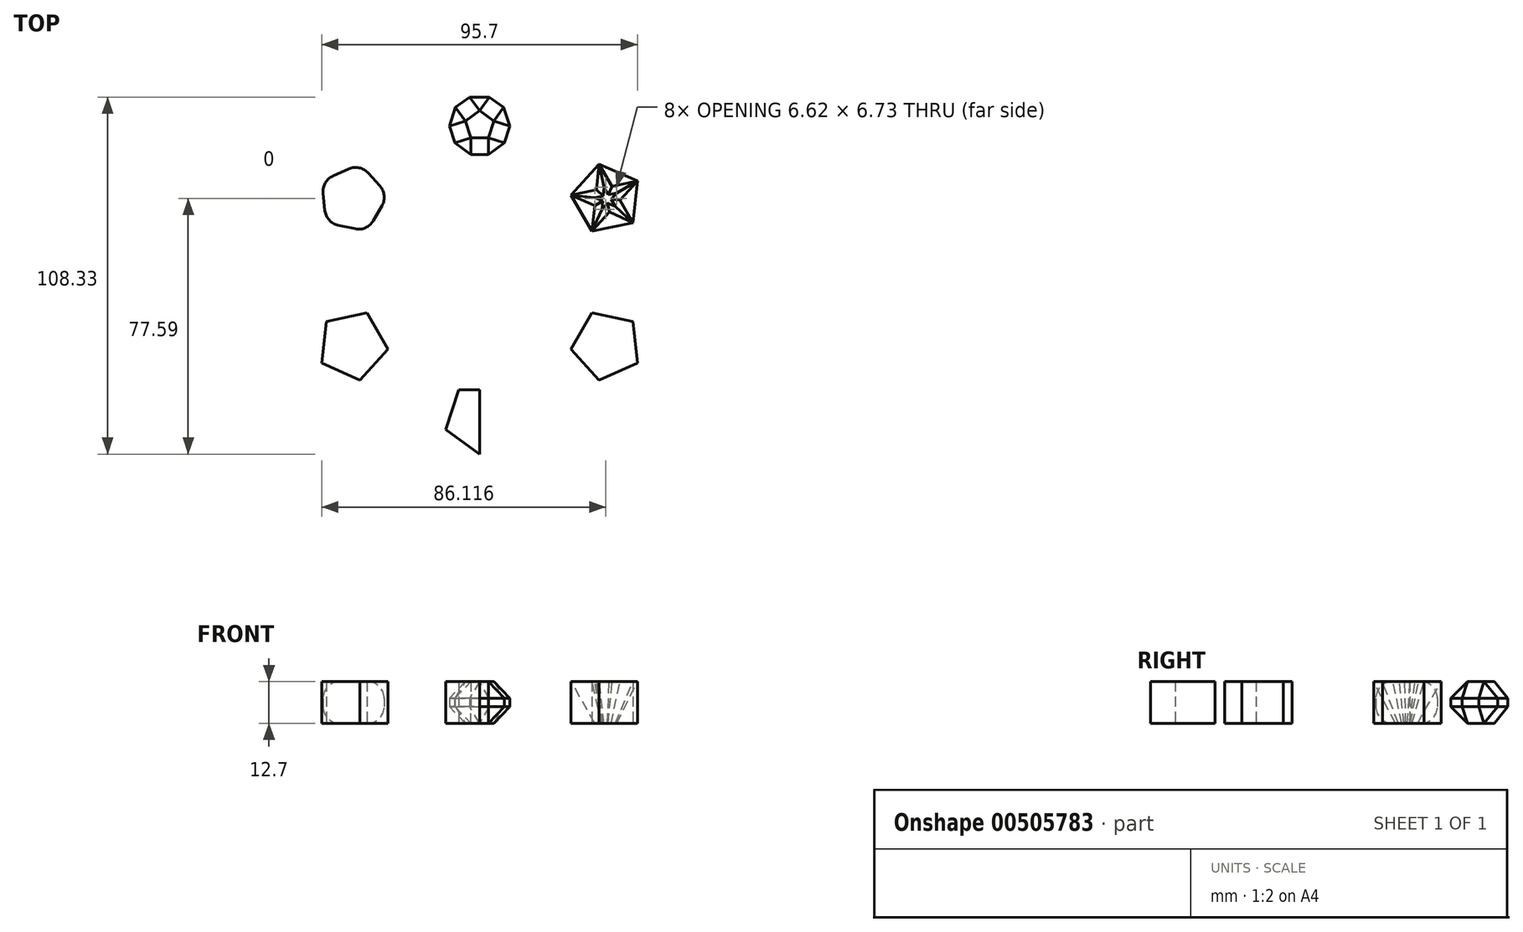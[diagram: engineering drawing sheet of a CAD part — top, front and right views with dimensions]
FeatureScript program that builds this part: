
annotation { "Feature Type Name" : "Feature", "Feature Type Description" : "" }
export const myFeature = defineFeature(function(context is Context, id is Id, definition is map)
    precondition{}
    {
        {
            var Q0;
            Q0=qCreatedBy(makeId("Top.planeOp"),FACE);
            var sketch = newSketch(context, id + "F0", { "sketchPlane" : qUnion([Q0])});
            skCircle(sketch, "E0", {"center": v(0, 0) * mm, "radius": 44.45 * mm, "construction": true});
            skCircle(sketch, "E1.cCircle", {"center": v(0, 44.45) * mm, "radius": 10.8 * mm, "construction": true});
            skLineSegment(sketch, "E1.0", {"start": v(0, 55.25) * mm, "end": v(10.27, 47.79) * mm});
            skLineSegment(sketch, "E1.1", {"start": v(10.27, 47.79) * mm, "end": v(6.35, 35.7) * mm});
            skLineSegment(sketch, "E1.2", {"start": v(6.35, 35.7) * mm, "end": v(-6.35, 35.7) * mm});
            skLineSegment(sketch, "E1.3", {"start": v(-6.35, 35.7) * mm, "end": v(-10.27, 47.79) * mm});
            skLineSegment(sketch, "E1.4", {"start": v(-10.27, 47.79) * mm, "end": v(0, 55.25) * mm});
            skLineSegment(sketch, "E2.1.0", {"start": v(-47.85, 27.63) * mm, "end": v(-36.25, 32.8) * mm});
            skLineSegment(sketch, "E2.1.1", {"start": v(-46.52, 15) * mm, "end": v(-47.85, 27.63) * mm});
            skLineSegment(sketch, "E2.1.2", {"start": v(-34.1, 12.36) * mm, "end": v(-46.52, 15) * mm});
            skLineSegment(sketch, "E2.1.3", {"start": v(-27.75, 23.35) * mm, "end": v(-34.1, 12.36) * mm});
            skLineSegment(sketch, "E2.1.4", {"start": v(-36.25, 32.8) * mm, "end": v(-27.75, 23.35) * mm});
            skLineSegment(sketch, "E2.2.0", {"start": v(-47.85, -27.63) * mm, "end": v(-46.52, -15) * mm});
            skLineSegment(sketch, "E2.2.1", {"start": v(-36.25, -32.8) * mm, "end": v(-47.85, -27.63) * mm});
            skLineSegment(sketch, "E2.2.2", {"start": v(-27.75, -23.35) * mm, "end": v(-36.25, -32.8) * mm});
            skLineSegment(sketch, "E2.2.3", {"start": v(-34.1, -12.36) * mm, "end": v(-27.75, -23.35) * mm});
            skLineSegment(sketch, "E2.2.4", {"start": v(-46.52, -15) * mm, "end": v(-34.1, -12.36) * mm});
            skLineSegment(sketch, "E2.3.0", {"start": v(0, -55.25) * mm, "end": v(-10.27, -47.79) * mm});
            skLineSegment(sketch, "E2.3.4", {"start": v(-10.27, -47.79) * mm, "end": v(-6.35, -35.7) * mm});
            skLineSegment(sketch, "E2.4.0", {"start": v(47.85, -27.63) * mm, "end": v(36.25, -32.8) * mm});
            skLineSegment(sketch, "E2.4.1", {"start": v(46.52, -15) * mm, "end": v(47.85, -27.63) * mm});
            skLineSegment(sketch, "E2.4.2", {"start": v(34.1, -12.36) * mm, "end": v(46.52, -15) * mm});
            skLineSegment(sketch, "E2.4.3", {"start": v(27.75, -23.35) * mm, "end": v(34.1, -12.36) * mm});
            skLineSegment(sketch, "E2.4.4", {"start": v(36.25, -32.8) * mm, "end": v(27.75, -23.35) * mm});
            skLineSegment(sketch, "E2.5.0", {"start": v(47.85, 27.63) * mm, "end": v(46.52, 15) * mm});
            skLineSegment(sketch, "E2.5.1", {"start": v(36.25, 32.8) * mm, "end": v(47.85, 27.63) * mm});
            skLineSegment(sketch, "E2.5.2", {"start": v(27.75, 23.35) * mm, "end": v(36.25, 32.8) * mm});
            skLineSegment(sketch, "E2.5.3", {"start": v(34.1, 12.36) * mm, "end": v(27.75, 23.35) * mm});
            skLineSegment(sketch, "E2.5.4", {"start": v(46.52, 15) * mm, "end": v(34.1, 12.36) * mm});
            skLineSegment(sketch, "E3", {"start": v(0, -55.25) * mm, "end": v(0, -35.7) * mm});
            skLineSegment(sketch, "E4", {"start": v(-6.35, -35.7) * mm, "end": v(0, -35.7) * mm});
            skSolve(sketch);
        }
        {
            var Q0;
            Q0 = qSketchRegion(id + "F0", true);
            var Q1;
            Q1=sQuery(id+"F0.wireOp",EDGE,"E2.2.4");
            var Q2;
            Q2=sQuery(id+"F0.wireOp",EDGE,"E2.2.0");
            var Q3;
            Q3=sQuery(id+"F0.wireOp",EDGE,"E2.2.3");
            var Q4;
            Q4=sQuery(id+"F0.wireOp",EDGE,"E2.1.3");
            extrude(context, id + "F1", {"entities" : qUnion([Q0]), "surfaceEntities" : qUnion([Q1, Q2, Q3, Q4]), "depth" : 12.7 * mm});
        }
        {
            var Q0;
            Q0=makeQuery(id+"F1.opExtrude","CAP_EDGE",EDGE,{"disambiguationData":[OSD([sQuery(id+"F0.wireOp",EDGE,"E2.1.3")])],"isStart":false});
            var Q1;
            Q1=makeQuery(id+"F1.opExtrude","CAP_EDGE",EDGE,{"disambiguationData":[OSD([sQuery(id+"F0.wireOp",EDGE,"E2.1.2")])],"isStart":false});
            var Q2;
            Q2=makeQuery(id+"F1.opExtrude","CAP_EDGE",EDGE,{"disambiguationData":[OSD([sQuery(id+"F0.wireOp",EDGE,"E2.1.1")])],"isStart":false});
            var Q3;
            Q3=makeQuery(id+"F1.opExtrude","CAP_EDGE",EDGE,{"disambiguationData":[OSD([sQuery(id+"F0.wireOp",EDGE,"E2.1.0")])],"isStart":false});
            var Q4;
            Q4=makeQuery(id+"F1.opExtrude","CAP_EDGE",EDGE,{"disambiguationData":[OSD([sQuery(id+"F0.wireOp",EDGE,"E2.1.4")])],"isStart":false});
            var Q5;
            Q5=makeQuery(id+"F1.opExtrude","SWEPT_FACE",FACE,{"disambiguationData":[OSD([sQuery(id+"F0.wireOp",EDGE,"E2.1.2")])]});
            var Q6;
            Q6=makeQuery(id+"F1.opExtrude","CAP_EDGE",EDGE,{"disambiguationData":[OSD([sQuery(id+"F0.wireOp",EDGE,"E2.1.3")])],"isStart":true});
            var Q7;
            Q7=makeQuery(id+"F1.opExtrude","SWEPT_FACE",FACE,{"disambiguationData":[OSD([sQuery(id+"F0.wireOp",EDGE,"E2.1.1")])]});
            var Q8;
            Q8=makeQuery(id+"F1.opExtrude","SWEPT_FACE",FACE,{"disambiguationData":[OSD([sQuery(id+"F0.wireOp",EDGE,"E2.1.0")])]});
            var Q9;
            Q9=makeQuery(id+"F1.opExtrude","SWEPT_FACE",FACE,{"disambiguationData":[OSD([sQuery(id+"F0.wireOp",EDGE,"E2.1.4")])]});
            var Q10;
            Q10=makeQuery(id+"F1.opExtrude","CAP_FACE",FACE,{"disambiguationData":[OSD([sQuery(id+"F0.wireOp",EDGE,"E2.1.0"),sQuery(id+"F0.wireOp",EDGE,"E2.1.1"),sQuery(id+"F0.wireOp",EDGE,"E2.1.2"),sQuery(id+"F0.wireOp",EDGE,"E2.1.3"),sQuery(id+"F0.wireOp",EDGE,"E2.1.4")])],"isStart":true});
            fillet(context, id + "F2", {"entities" : qUnion([Q0, Q1, Q2, Q3, Q4, Q5, Q6, Q7, Q8, Q9, Q10]), "radius" : 5.08 * mm, "tangentPropagation" : true, "allowEdgeOverflow" : false});
        }
        {
            var Q0;
            Q0=makeQuery(id+"F1.opExtrude","CAP_FACE",FACE,{"disambiguationData":[OSD([sQuery(id+"F0.wireOp",EDGE,"E1.0"),sQuery(id+"F0.wireOp",EDGE,"E1.1"),sQuery(id+"F0.wireOp",EDGE,"E1.2"),sQuery(id+"F0.wireOp",EDGE,"E1.3"),sQuery(id+"F0.wireOp",EDGE,"E1.4")])],"isStart":false});
            var Q1;
            Q1=makeQuery(id+"F1.opExtrude","CAP_FACE",FACE,{"disambiguationData":[OSD([sQuery(id+"F0.wireOp",EDGE,"E1.0"),sQuery(id+"F0.wireOp",EDGE,"E1.1"),sQuery(id+"F0.wireOp",EDGE,"E1.2"),sQuery(id+"F0.wireOp",EDGE,"E1.3"),sQuery(id+"F0.wireOp",EDGE,"E1.4")])],"isStart":true});
            var Q2;
            Q2=makeQuery(id+"F1.opExtrude","SWEPT_FACE",FACE,{"disambiguationData":[OSD([sQuery(id+"F0.wireOp",EDGE,"E1.2")])]});
            var Q3;
            Q3=makeQuery(id+"F1.opExtrude","SWEPT_EDGE",EDGE,{"disambiguationData":[OSD([sQuery(id+"F0.wireOp",EDGE,"E1.0"),sQuery(id+"F0.wireOp",EDGE,"E1.1")])]});
            var Q4;
            Q4=makeQuery(id+"F1.opExtrude","SWEPT_FACE",FACE,{"disambiguationData":[OSD([sQuery(id+"F0.wireOp",EDGE,"E1.1")])]});
            var Q5;
            Q5=makeQuery(id+"F1.opExtrude","SWEPT_FACE",FACE,{"disambiguationData":[OSD([sQuery(id+"F0.wireOp",EDGE,"E1.0")])]});
            var Q6;
            Q6=makeQuery(id+"F1.opExtrude","SWEPT_FACE",FACE,{"disambiguationData":[OSD([sQuery(id+"F0.wireOp",EDGE,"E1.4")])]});
            chamfer(context, id + "F3", {"entities" : qUnion([Q0, Q1, Q2, Q3, Q4, Q5, Q6]), "width" : 5.08 * mm, "tangentPropagation" : true});
        }
        {
            var Q0;
            Q0=makeQuery(id+"F1.opExtrude","CAP_FACE",FACE,{"disambiguationData":[OSD([sQuery(id+"F0.wireOp",EDGE,"E2.5.0"),sQuery(id+"F0.wireOp",EDGE,"E2.5.1"),sQuery(id+"F0.wireOp",EDGE,"E2.5.2"),sQuery(id+"F0.wireOp",EDGE,"E2.5.3"),sQuery(id+"F0.wireOp",EDGE,"E2.5.4")])],"isStart":false});
            var sketch = newSketch(context, id + "F4", { "sketchPlane" : qUnion([Q0])});
            skLineSegment(sketch, "E5", {"start": v(27.75, 23.35) * mm, "end": v(47.85, 27.63) * mm});
            skLineSegment(sketch, "E6", {"start": v(47.85, 27.63) * mm, "end": v(34.1, 12.36) * mm});
            skLineSegment(sketch, "E7", {"start": v(34.1, 12.36) * mm, "end": v(36.25, 32.8) * mm});
            skLineSegment(sketch, "E8", {"start": v(36.25, 32.8) * mm, "end": v(46.52, 15) * mm});
            skLineSegment(sketch, "E9", {"start": v(46.52, 15) * mm, "end": v(27.75, 23.35) * mm});
            skLineSegment(sketch, "E10", {"start": v(35.43, 24.99) * mm, "end": v(42.6, 21.8) * mm});
            skLineSegment(sketch, "E11", {"start": v(42.6, 21.8) * mm, "end": v(34.92, 20.16) * mm});
            skLineSegment(sketch, "E12", {"start": v(34.92, 20.16) * mm, "end": v(40.17, 26) * mm});
            skLineSegment(sketch, "E13", {"start": v(40.17, 26) * mm, "end": v(39.35, 18.19) * mm});
            skLineSegment(sketch, "E14", {"start": v(39.35, 18.19) * mm, "end": v(35.43, 24.99) * mm});
            skSolve(sketch);
        }
        {
            var Q0;
            {var subQ0=sQuery(id+"F4.wireOp",EDGE,"E7");var subQ1=sQuery(id+"F4.wireOp",EDGE,"E5");var subQ2=makeQuery(id+"F4.imprint","INTERSECT",VERTEX,{"derivedFrom":[subQ1,subQ0,sQuery(id+"F4.wireOp",EDGE,"E10"),sQuery(id+"F4.wireOp",EDGE,"E14")]});Q0=makeQuery(id+"F4.imprint","IMPRINT",FACE,{"disambiguationData":[TD([[makeQuery(id+"F4.imprint","IMPRINT",EDGE,{"disambiguationData":[TD([[subQ2,-1.0]])],"derivedFrom":subQ1}),1.0]])]});}
            var Q1;
            {var subQ0=sQuery(id+"F4.wireOp",EDGE,"E10");var subQ3=sQuery(id+"F4.wireOp",EDGE,"E12");var subQ5=makeQuery(id+"F4.imprint","INTERSECT",VERTEX,{"derivedFrom":[subQ0,subQ3]});Q1=makeQuery(id+"F4.imprint","IMPRINT",FACE,{"disambiguationData":[TD([[makeQuery(id+"F4.imprint","IMPRINT",EDGE,{"disambiguationData":[TD([[subQ5,1.0]])],"derivedFrom":subQ0}),1.0]])]});}
            var Q2;
            {var subQ1=sQuery(id+"F4.wireOp",EDGE,"E10");var subQ3=sQuery(id+"F4.wireOp",EDGE,"E12");var subQ4=makeQuery(id+"F4.imprint","INTERSECT",VERTEX,{"derivedFrom":[subQ1,subQ3]});Q2=makeQuery(id+"F4.imprint","IMPRINT",FACE,{"disambiguationData":[TD([[makeQuery(id+"F4.imprint","IMPRINT",EDGE,{"disambiguationData":[TD([[subQ4,1.0]])],"derivedFrom":subQ3}),1.0]])]});}
            var Q3;
            {var subQ0=sQuery(id+"F4.wireOp",EDGE,"E12");var subQ1=sQuery(id+"F4.wireOp",EDGE,"E10");var subQ2=makeQuery(id+"F4.imprint","INTERSECT",VERTEX,{"derivedFrom":[subQ1,subQ0]});Q3=makeQuery(id+"F4.imprint","IMPRINT",FACE,{"disambiguationData":[TD([[makeQuery(id+"F4.imprint","IMPRINT",EDGE,{"disambiguationData":[TD([[subQ2,-1.0]])],"derivedFrom":subQ1}),1.0]])]});}
            var Q4;
            {var subQ1=sQuery(id+"F4.wireOp",EDGE,"E10");var subQ5=sQuery(id+"F4.wireOp",EDGE,"E12");var subQ6=makeQuery(id+"F4.imprint","INTERSECT",VERTEX,{"derivedFrom":[subQ1,subQ5]});Q4=makeQuery(id+"F4.imprint","IMPRINT",FACE,{"disambiguationData":[TD([[makeQuery(id+"F4.imprint","IMPRINT",EDGE,{"disambiguationData":[TD([[subQ6,-1.0]])],"derivedFrom":subQ1}),-1.0]])]});}
            var Q5;
            {var subQ1=sQuery(id+"F4.wireOp",EDGE,"E11");var subQ3=sQuery(id+"F4.wireOp",EDGE,"E14");var subQ4=makeQuery(id+"F4.imprint","INTERSECT",VERTEX,{"derivedFrom":[subQ1,subQ3]});Q5=makeQuery(id+"F4.imprint","IMPRINT",FACE,{"disambiguationData":[TD([[makeQuery(id+"F4.imprint","IMPRINT",EDGE,{"disambiguationData":[TD([[subQ4,-1.0]])],"derivedFrom":subQ3}),1.0]])]});}
            var Q6;
            {var subQ1=sQuery(id+"F4.wireOp",EDGE,"E10");var subQ3=sQuery(id+"F4.wireOp",EDGE,"E13");var subQ4=makeQuery(id+"F4.imprint","INTERSECT",VERTEX,{"derivedFrom":[subQ1,subQ3]});Q6=makeQuery(id+"F4.imprint","IMPRINT",FACE,{"disambiguationData":[TD([[makeQuery(id+"F4.imprint","IMPRINT",EDGE,{"disambiguationData":[TD([[subQ4,-1.0]])],"derivedFrom":subQ3}),1.0]])]});}
            var Q7;
            {var subQ0=sQuery(id+"F4.wireOp",EDGE,"E13");var subQ1=sQuery(id+"F4.wireOp",EDGE,"E11");var subQ2=makeQuery(id+"F4.imprint","INTERSECT",VERTEX,{"derivedFrom":[subQ1,subQ0]});Q7=makeQuery(id+"F4.imprint","IMPRINT",FACE,{"disambiguationData":[TD([[makeQuery(id+"F4.imprint","IMPRINT",EDGE,{"disambiguationData":[TD([[subQ2,-1.0]])],"derivedFrom":subQ1}),1.0]])]});}
            var Q8;
            {var subQ0=sQuery(id+"F4.wireOp",EDGE,"E14");var subQ3=sQuery(id+"F4.wireOp",EDGE,"E12");var subQ5=makeQuery(id+"F4.imprint","INTERSECT",VERTEX,{"derivedFrom":[subQ3,subQ0]});Q8=makeQuery(id+"F4.imprint","IMPRINT",FACE,{"disambiguationData":[TD([[makeQuery(id+"F4.imprint","IMPRINT",EDGE,{"disambiguationData":[TD([[subQ5,1.0]])],"derivedFrom":subQ3}),1.0]])]});}
            var Q9;
            {var subQ0=sQuery(id+"F4.wireOp",EDGE,"E11");var subQ3=sQuery(id+"F4.wireOp",EDGE,"E14");var subQ5=makeQuery(id+"F4.imprint","INTERSECT",VERTEX,{"derivedFrom":[subQ0,subQ3]});Q9=makeQuery(id+"F4.imprint","IMPRINT",FACE,{"disambiguationData":[TD([[makeQuery(id+"F4.imprint","IMPRINT",EDGE,{"disambiguationData":[TD([[subQ5,-1.0]])],"derivedFrom":subQ0}),1.0]])]});}
            var Q10;
            {var subQ0=sQuery(id+"F4.wireOp",EDGE,"E11");var subQ3=sQuery(id+"F4.wireOp",EDGE,"E13");var subQ5=makeQuery(id+"F4.imprint","INTERSECT",VERTEX,{"derivedFrom":[subQ0,subQ3]});Q10=makeQuery(id+"F4.imprint","IMPRINT",FACE,{"disambiguationData":[TD([[makeQuery(id+"F4.imprint","IMPRINT",EDGE,{"disambiguationData":[TD([[subQ5,1.0]])],"derivedFrom":subQ0}),1.0]])]});}
            var Q11;
            {var subQ0=sQuery(id+"F4.wireOp",EDGE,"E10");var subQ3=sQuery(id+"F4.wireOp",EDGE,"E13");var subQ5=makeQuery(id+"F4.imprint","INTERSECT",VERTEX,{"derivedFrom":[subQ0,subQ3]});Q11=makeQuery(id+"F4.imprint","IMPRINT",FACE,{"disambiguationData":[TD([[makeQuery(id+"F4.imprint","IMPRINT",EDGE,{"disambiguationData":[TD([[subQ5,-1.0]])],"derivedFrom":subQ0}),1.0]])]});}
            var Q12;
            {var subQ0=sQuery(id+"F4.wireOp",EDGE,"E6");var subQ1=sQuery(id+"F4.wireOp",EDGE,"E5");var subQ2=makeQuery(id+"F4.imprint","INTERSECT",VERTEX,{"derivedFrom":[makeQuery(id+"F1.opExtrude","CAP_EDGE",EDGE,{"disambiguationData":[OSD([sQuery(id+"F0.wireOp",EDGE,"E2.5.0")])],"isStart":false}),makeQuery(id+"F1.opExtrude","CAP_EDGE",EDGE,{"disambiguationData":[OSD([sQuery(id+"F0.wireOp",EDGE,"E2.5.1")])],"isStart":false}),subQ1,subQ0]});Q12=makeQuery(id+"F4.imprint","IMPRINT",FACE,{"disambiguationData":[TD([[makeQuery(id+"F4.imprint","IMPRINT",EDGE,{"disambiguationData":[TD([[subQ2,1.0]])],"derivedFrom":subQ1}),-1.0]])]});}
            var Q13;
            {var subQ0=sQuery(id+"F4.wireOp",EDGE,"E8");var subQ1=sQuery(id+"F4.wireOp",EDGE,"E6");var subQ2=makeQuery(id+"F4.imprint","INTERSECT",VERTEX,{"derivedFrom":[subQ1,subQ0,sQuery(id+"F4.wireOp",EDGE,"E10"),sQuery(id+"F4.wireOp",EDGE,"E11")]});Q13=makeQuery(id+"F4.imprint","IMPRINT",FACE,{"disambiguationData":[TD([[makeQuery(id+"F4.imprint","IMPRINT",EDGE,{"disambiguationData":[TD([[subQ2,-1.0]])],"derivedFrom":subQ1}),1.0]])]});}
            var Q14;
            {var subQ0=sQuery(id+"F4.wireOp",EDGE,"E7");var subQ1=sQuery(id+"F4.wireOp",EDGE,"E6");var subQ2=makeQuery(id+"F4.imprint","INTERSECT",VERTEX,{"derivedFrom":[makeQuery(id+"F1.opExtrude","CAP_EDGE",EDGE,{"disambiguationData":[OSD([sQuery(id+"F0.wireOp",EDGE,"E2.5.3")])],"isStart":false}),makeQuery(id+"F1.opExtrude","CAP_EDGE",EDGE,{"disambiguationData":[OSD([sQuery(id+"F0.wireOp",EDGE,"E2.5.4")])],"isStart":false}),subQ1,subQ0]});Q14=makeQuery(id+"F4.imprint","IMPRINT",FACE,{"disambiguationData":[TD([[makeQuery(id+"F4.imprint","IMPRINT",EDGE,{"disambiguationData":[TD([[subQ2,1.0]])],"derivedFrom":subQ1}),-1.0]])]});}
            var Q15;
            {var subQ0=sQuery(id+"F4.wireOp",EDGE,"E9");var subQ1=sQuery(id+"F4.wireOp",EDGE,"E5");var subQ2=makeQuery(id+"F4.imprint","INTERSECT",VERTEX,{"derivedFrom":[makeQuery(id+"F1.opExtrude","CAP_EDGE",EDGE,{"disambiguationData":[OSD([sQuery(id+"F0.wireOp",EDGE,"E2.5.2")])],"isStart":false}),makeQuery(id+"F1.opExtrude","CAP_EDGE",EDGE,{"disambiguationData":[OSD([sQuery(id+"F0.wireOp",EDGE,"E2.5.3")])],"isStart":false}),subQ1,subQ0]});Q15=makeQuery(id+"F4.imprint","IMPRINT",FACE,{"disambiguationData":[TD([[makeQuery(id+"F4.imprint","IMPRINT",EDGE,{"disambiguationData":[TD([[subQ2,-1.0]])],"derivedFrom":subQ1}),-1.0]])]});}
            extrude(context, id + "F5", {"entities" : qUnion([Q0, Q1, Q2, Q3, Q4, Q5, Q6, Q7, Q8, Q9, Q10, Q11, Q12, Q13, Q14, Q15]), "operationType" : NewBodyOperationType.REMOVE, "oppositeDirection" : true, "depth" : 25.4 * mm, "hasDraft" : true, "draftAngle" : 10 * degree, "draftPullDirection" : true});
        }
    });
